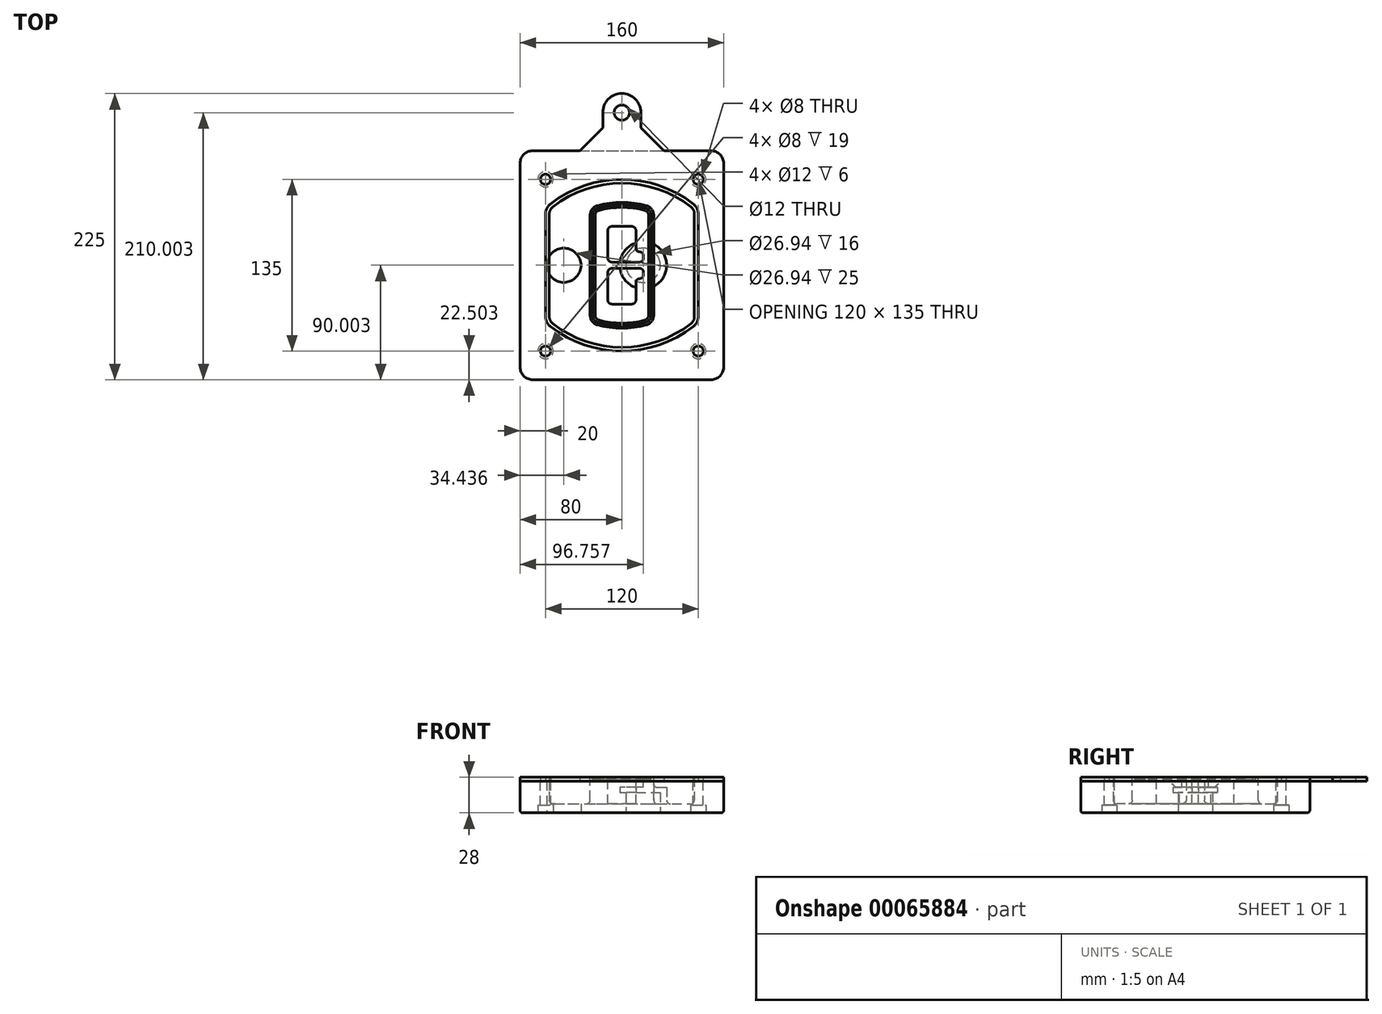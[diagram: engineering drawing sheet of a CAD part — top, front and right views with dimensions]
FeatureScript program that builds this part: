
annotation { "Feature Type Name" : "Feature", "Feature Type Description" : "" }
export const myFeature = defineFeature(function(context is Context, id is Id, definition is map)
    precondition{}
    {
        {
            var Q0;
            Q0=qCreatedBy(makeId("Top.planeOp"),FACE);
            var sketch = newSketch(context, id + "F0", { "sketchPlane" : qUnion([Q0])});
            skPoint(sketch, "E0.rect.middle", {"position": v(0, 0) * mm});
            skLineSegment(sketch, "E1.bottom", {"start": v(24.05, 28.38) * mm, "end": v(164.05, 28.38) * mm});
            skLineSegment(sketch, "E1.top", {"start": v(24.05, 208.38) * mm, "end": v(164.05, 208.38) * mm});
            skLineSegment(sketch, "E1.left", {"start": v(14.05, 38.38) * mm, "end": v(14.05, 198.38) * mm});
            skLineSegment(sketch, "E1.right", {"start": v(174.05, 38.38) * mm, "end": v(174.05, 198.38) * mm});
            skLineSegment(sketch, "E2", {"start": v(14.05, 208.38) * mm, "end": v(174.05, 28.38) * mm, "construction": true});
            skLineSegment(sketch, "E3", {"start": v(174.05, 208.38) * mm, "end": v(14.05, 28.38) * mm, "construction": true});
            skCircle(sketch, "E4", {"center": v(34.05, 185.88) * mm, "radius": 4 * mm});
            skCircle(sketch, "E5", {"center": v(154.05, 185.88) * mm, "radius": 4 * mm});
            skCircle(sketch, "E6", {"center": v(154.05, 50.88) * mm, "radius": 4 * mm});
            skCircle(sketch, "E7", {"center": v(34.05, 50.88) * mm, "radius": 4 * mm});
            skLineSegment(sketch, "E8", {"start": v(34.05, 185.88) * mm, "end": v(154.05, 185.88) * mm, "construction": true});
            skLineSegment(sketch, "E9", {"start": v(154.05, 185.88) * mm, "end": v(154.05, 50.88) * mm, "construction": true});
            skLineSegment(sketch, "E10", {"start": v(154.05, 50.88) * mm, "end": v(34.05, 50.88) * mm, "construction": true});
            skLineSegment(sketch, "E11", {"start": v(34.05, 50.88) * mm, "end": v(34.05, 185.88) * mm, "construction": true});
            skLineSegment(sketch, "E12", {"start": v(34.05, 158.68) * mm, "end": v(34.05, 78.09) * mm});
            skLineSegment(sketch, "E13", {"start": v(154.05, 158.68) * mm, "end": v(154.05, 78.09) * mm});
            skArc(sketch, "E14", {"start": v(150.2, 166.56) * mm, "mid": v(94.05, 185.88) * mm, "end": v(37.9, 166.56) * mm});
            skArc(sketch, "E15", {"start": v(37.9, 70.2) * mm, "mid": v(94.05, 50.88) * mm, "end": v(150.2, 70.2) * mm});
            skLineSegment(sketch, "E16", {"start": v(34.05, 118.38) * mm, "end": v(154.05, 118.38) * mm, "construction": true});
            skPoint(sketch, "E17.visualSharp", {"position": v(34.05, 73.38) * mm});
            skArc(sketch, "E17.filletArc", {"start": v(34.05, 78.09) * mm, "mid": v(35.06, 73.7) * mm, "end": v(37.9, 70.2) * mm});
            skPoint(sketch, "E18.visualSharp", {"position": v(34.05, 163.38) * mm});
            skArc(sketch, "E18.filletArc", {"start": v(37.9, 166.56) * mm, "mid": v(35.06, 163.06) * mm, "end": v(34.05, 158.68) * mm});
            skPoint(sketch, "E19.visualSharp", {"position": v(154.05, 163.38) * mm});
            skArc(sketch, "E19.filletArc", {"start": v(154.05, 158.68) * mm, "mid": v(153.04, 163.06) * mm, "end": v(150.2, 166.56) * mm});
            skPoint(sketch, "E20.visualSharp", {"position": v(154.05, 73.38) * mm});
            skArc(sketch, "E20.filletArc", {"start": v(150.2, 70.2) * mm, "mid": v(153.04, 73.7) * mm, "end": v(154.05, 78.09) * mm});
            skPoint(sketch, "E21.visualSharp", {"position": v(14.05, 208.38) * mm});
            skArc(sketch, "E21.filletArc", {"start": v(24.05, 208.38) * mm, "mid": v(16.98, 205.45) * mm, "end": v(14.05, 198.38) * mm});
            skPoint(sketch, "E22.visualSharp", {"position": v(174.05, 208.38) * mm});
            skArc(sketch, "E22.filletArc", {"start": v(174.05, 198.38) * mm, "mid": v(171.12, 205.45) * mm, "end": v(164.05, 208.38) * mm});
            skPoint(sketch, "E23.visualSharp", {"position": v(174.05, 28.38) * mm});
            skArc(sketch, "E23.filletArc", {"start": v(164.05, 28.38) * mm, "mid": v(171.12, 31.31) * mm, "end": v(174.05, 38.38) * mm});
            skPoint(sketch, "E24.visualSharp", {"position": v(14.05, 28.38) * mm});
            skArc(sketch, "E24.filletArc", {"start": v(14.05, 38.38) * mm, "mid": v(16.98, 31.31) * mm, "end": v(24.05, 28.38) * mm});
            skArc(sketch, "E25.0", {"start": v(151.05, 158.68) * mm, "mid": v(150.34, 161.75) * mm, "end": v(148.36, 164.2) * mm});
            skLineSegment(sketch, "E25.1", {"start": v(151.05, 158.68) * mm, "end": v(151.05, 78.09) * mm});
            skArc(sketch, "E25.2", {"start": v(148.36, 72.57) * mm, "mid": v(150.34, 75.02) * mm, "end": v(151.05, 78.09) * mm});
            skArc(sketch, "E25.3", {"start": v(39.74, 72.57) * mm, "mid": v(94.05, 53.88) * mm, "end": v(148.36, 72.57) * mm});
            skArc(sketch, "E25.4", {"start": v(37.05, 78.09) * mm, "mid": v(37.76, 75.02) * mm, "end": v(39.74, 72.57) * mm});
            skArc(sketch, "E25.5", {"start": v(148.36, 164.2) * mm, "mid": v(94.05, 182.88) * mm, "end": v(39.74, 164.2) * mm});
            skLineSegment(sketch, "E25.6", {"start": v(37.05, 158.68) * mm, "end": v(37.05, 78.09) * mm});
            skArc(sketch, "E25.7", {"start": v(39.74, 164.2) * mm, "mid": v(37.76, 161.75) * mm, "end": v(37.05, 158.68) * mm});
            skArc(sketch, "E26.0", {"start": v(35.43, 169.71) * mm, "mid": v(31.47, 164.82) * mm, "end": v(30.05, 158.68) * mm});
            skArc(sketch, "E26.1", {"start": v(152.67, 169.71) * mm, "mid": v(94.05, 189.88) * mm, "end": v(35.43, 169.71) * mm});
            skArc(sketch, "E26.2", {"start": v(158.05, 158.68) * mm, "mid": v(156.63, 164.82) * mm, "end": v(152.67, 169.71) * mm});
            skLineSegment(sketch, "E26.3", {"start": v(158.05, 158.68) * mm, "end": v(158.05, 78.09) * mm});
            skArc(sketch, "E26.4", {"start": v(152.67, 67.05) * mm, "mid": v(156.63, 71.95) * mm, "end": v(158.05, 78.09) * mm});
            skLineSegment(sketch, "E26.5", {"start": v(30.05, 158.68) * mm, "end": v(30.05, 78.09) * mm});
            skArc(sketch, "E26.6", {"start": v(35.43, 67.05) * mm, "mid": v(94.05, 46.88) * mm, "end": v(152.67, 67.05) * mm});
            skArc(sketch, "E26.7", {"start": v(30.05, 78.09) * mm, "mid": v(31.47, 71.95) * mm, "end": v(35.43, 67.05) * mm});
            skSolve(sketch);
        }
        {
            var Q0;
            Q0=makeQuery(id+"F0.imprint","IMPRINT",FACE,{"disambiguationData":[TD([[makeQuery(id+"F0.imprint","IMPRINT",EDGE,{"derivedFrom":sQuery(id+"F0.wireOp",EDGE,"E1.bottom")}),1.0]])]});
            var Q1;
            Q1=makeQuery(id+"F0.imprint","IMPRINT",FACE,{"disambiguationData":[TD([[makeQuery(id+"F0.imprint","IMPRINT",EDGE,{"derivedFrom":sQuery(id+"F0.wireOp",EDGE,"E12")}),1.0]])]});
            var Q2;
            Q2=makeQuery(id+"F0.imprint","IMPRINT",FACE,{"disambiguationData":[TD([[makeQuery(id+"F0.imprint","IMPRINT",EDGE,{"derivedFrom":sQuery(id+"F0.wireOp",EDGE,"E25.0")}),1.0]])]});
            var Q3;
            Q3=makeQuery(id+"F0.imprint","IMPRINT",FACE,{"disambiguationData":[TD([[makeQuery(id+"F0.imprint","IMPRINT",EDGE,{"derivedFrom":sQuery(id+"F0.wireOp",EDGE,"E12")}),-1.0]])]});
            extrude(context, id + "F1", {"entities" : qUnion([Q0, Q1, Q2, Q3]), "oppositeDirection" : true, "depth" : 25 * mm});
        }
        {
            var Q0;
            Q0=makeQuery(id+"F0.imprint","IMPRINT",FACE,{"disambiguationData":[TD([[makeQuery(id+"F0.imprint","IMPRINT",EDGE,{"derivedFrom":sQuery(id+"F0.wireOp",EDGE,"E12")}),1.0]])]});
            extrude(context, id + "F2", {"entities" : qUnion([Q0]), "operationType" : NewBodyOperationType.ADD, "depth" : 3 * mm});
        }
        {
            var Q0;
            Q0=makeQuery(id+"F0.imprint","IMPRINT",FACE,{"disambiguationData":[TD([[makeQuery(id+"F0.imprint","IMPRINT",EDGE,{"derivedFrom":sQuery(id+"F0.wireOp",EDGE,"E25.0")}),1.0]])]});
            extrude(context, id + "F3", {"entities" : qUnion([Q0]), "operationType" : NewBodyOperationType.REMOVE, "oppositeDirection" : true, "depth" : 18 * mm});
        }
        {
            var Q0;
            Q0=makeQuery(id+"F2.opExtrude","CAP_FACE",FACE,{"disambiguationData":[OSD([sQuery(id+"F0.wireOp",EDGE,"E12"),sQuery(id+"F0.wireOp",EDGE,"E13"),sQuery(id+"F0.wireOp",EDGE,"E14"),sQuery(id+"F0.wireOp",EDGE,"E15"),sQuery(id+"F0.wireOp",EDGE,"E17.filletArc"),sQuery(id+"F0.wireOp",EDGE,"E18.filletArc"),sQuery(id+"F0.wireOp",EDGE,"E19.filletArc"),sQuery(id+"F0.wireOp",EDGE,"E20.filletArc"),sQuery(id+"F0.wireOp",EDGE,"E25.0"),sQuery(id+"F0.wireOp",EDGE,"E25.1"),sQuery(id+"F0.wireOp",EDGE,"E25.2"),sQuery(id+"F0.wireOp",EDGE,"E25.3"),sQuery(id+"F0.wireOp",EDGE,"E25.4"),sQuery(id+"F0.wireOp",EDGE,"E25.5"),sQuery(id+"F0.wireOp",EDGE,"E25.6"),sQuery(id+"F0.wireOp",EDGE,"E25.7")])],"isStart":false});
            var sketch = newSketch(context, id + "F4", { "sketchPlane" : qUnion([Q0])});
            skArc(sketch, "E27.0", {"start": v(74.97, 71.41) * mm, "mid": v(94.05, 68.88) * mm, "end": v(113.13, 71.41) * mm});
            skArc(sketch, "E28.0", {"start": v(113.13, 165.35) * mm, "mid": v(94.05, 167.88) * mm, "end": v(74.97, 165.35) * mm});
            skLineSegment(sketch, "E29", {"start": v(69.05, 157.63) * mm, "end": v(69.05, 79.14) * mm});
            skLineSegment(sketch, "E30", {"start": v(119.05, 157.63) * mm, "end": v(119.05, 79.14) * mm});
            skLineSegment(sketch, "E31", {"start": v(69.05, 163.48) * mm, "end": v(119.05, 163.48) * mm, "construction": true});
            skLineSegment(sketch, "E32", {"start": v(69.05, 73.28) * mm, "end": v(119.05, 73.28) * mm, "construction": true});
            skPoint(sketch, "E33.visualSharp", {"position": v(69.05, 163.48) * mm});
            skArc(sketch, "E33.filletArc", {"start": v(74.97, 165.35) * mm, "mid": v(70.7, 162.5) * mm, "end": v(69.05, 157.63) * mm});
            skPoint(sketch, "E34.visualSharp", {"position": v(119.05, 163.48) * mm});
            skArc(sketch, "E34.filletArc", {"start": v(119.05, 157.63) * mm, "mid": v(117.4, 162.5) * mm, "end": v(113.13, 165.35) * mm});
            skPoint(sketch, "E35.visualSharp", {"position": v(119.05, 73.28) * mm});
            skArc(sketch, "E35.filletArc", {"start": v(113.13, 71.41) * mm, "mid": v(117.4, 74.27) * mm, "end": v(119.05, 79.14) * mm});
            skPoint(sketch, "E36.visualSharp", {"position": v(69.05, 73.28) * mm});
            skArc(sketch, "E36.filletArc", {"start": v(69.05, 79.14) * mm, "mid": v(70.7, 74.27) * mm, "end": v(74.97, 71.41) * mm});
            skArc(sketch, "E37.0", {"start": v(148.36, 164.2) * mm, "mid": v(94.05, 182.88) * mm, "end": v(39.74, 164.2) * mm});
            skArc(sketch, "E37.1", {"start": v(39.74, 164.2) * mm, "mid": v(37.76, 161.75) * mm, "end": v(37.05, 158.68) * mm});
            skLineSegment(sketch, "E37.2", {"start": v(37.05, 158.68) * mm, "end": v(37.05, 78.09) * mm});
            skArc(sketch, "E37.3", {"start": v(37.05, 78.09) * mm, "mid": v(37.76, 75.02) * mm, "end": v(39.74, 72.57) * mm});
            skArc(sketch, "E37.4", {"start": v(39.74, 72.57) * mm, "mid": v(94.05, 53.88) * mm, "end": v(148.36, 72.57) * mm});
            skArc(sketch, "E37.5", {"start": v(148.36, 72.57) * mm, "mid": v(150.34, 75.02) * mm, "end": v(151.05, 78.09) * mm});
            skLineSegment(sketch, "E37.6", {"start": v(151.05, 158.68) * mm, "end": v(151.05, 78.09) * mm});
            skArc(sketch, "E37.7", {"start": v(151.05, 158.68) * mm, "mid": v(150.34, 161.75) * mm, "end": v(148.36, 164.2) * mm});
            skLineSegment(sketch, "E38.0", {"start": v(117.05, 157.63) * mm, "end": v(117.05, 79.14) * mm});
            skArc(sketch, "E38.1", {"start": v(112.61, 73.34) * mm, "mid": v(115.81, 75.49) * mm, "end": v(117.05, 79.14) * mm});
            skArc(sketch, "E38.2", {"start": v(75.49, 73.34) * mm, "mid": v(94.05, 70.88) * mm, "end": v(112.61, 73.34) * mm});
            skArc(sketch, "E38.3", {"start": v(71.05, 79.14) * mm, "mid": v(72.29, 75.49) * mm, "end": v(75.49, 73.34) * mm});
            skLineSegment(sketch, "E38.4", {"start": v(71.05, 157.63) * mm, "end": v(71.05, 79.14) * mm});
            skArc(sketch, "E38.5", {"start": v(117.05, 157.63) * mm, "mid": v(115.81, 161.28) * mm, "end": v(112.61, 163.42) * mm});
            skArc(sketch, "E38.6", {"start": v(75.49, 163.42) * mm, "mid": v(72.29, 161.28) * mm, "end": v(71.05, 157.63) * mm});
            skArc(sketch, "E38.7", {"start": v(112.61, 163.42) * mm, "mid": v(94.05, 165.88) * mm, "end": v(75.49, 163.42) * mm});
            skArc(sketch, "E39.0", {"start": v(115.05, 157.63) * mm, "mid": v(114.23, 160.06) * mm, "end": v(112.1, 161.5) * mm});
            skLineSegment(sketch, "E39.1", {"start": v(115.05, 157.63) * mm, "end": v(115.05, 79.14) * mm});
            skArc(sketch, "E39.2", {"start": v(112.1, 75.27) * mm, "mid": v(114.23, 76.7) * mm, "end": v(115.05, 79.14) * mm});
            skArc(sketch, "E39.3", {"start": v(76, 75.27) * mm, "mid": v(94.05, 72.88) * mm, "end": v(112.1, 75.27) * mm});
            skArc(sketch, "E39.4", {"start": v(73.05, 79.14) * mm, "mid": v(73.87, 76.7) * mm, "end": v(76, 75.27) * mm});
            skArc(sketch, "E39.5", {"start": v(112.1, 161.5) * mm, "mid": v(94.05, 163.88) * mm, "end": v(76, 161.5) * mm});
            skLineSegment(sketch, "E39.6", {"start": v(73.05, 157.63) * mm, "end": v(73.05, 79.14) * mm});
            skArc(sketch, "E39.7", {"start": v(76, 161.5) * mm, "mid": v(73.87, 160.06) * mm, "end": v(73.05, 157.63) * mm});
            skLineSegment(sketch, "E40", {"start": v(69.05, 118.38) * mm, "end": v(119.05, 118.38) * mm, "construction": true});
            skLineSegment(sketch, "E41", {"start": v(83.05, 123.88) * mm, "end": v(83.05, 145.88) * mm});
            skLineSegment(sketch, "E42", {"start": v(86.05, 148.88) * mm, "end": v(102.05, 148.88) * mm});
            skLineSegment(sketch, "E43", {"start": v(105.05, 145.88) * mm, "end": v(105.05, 131.88) * mm});
            skLineSegment(sketch, "E44", {"start": v(108.05, 128.88) * mm, "end": v(108.05, 128.88) * mm});
            skLineSegment(sketch, "E45", {"start": v(111.05, 125.88) * mm, "end": v(111.05, 123.88) * mm});
            skLineSegment(sketch, "E46", {"start": v(108.05, 120.88) * mm, "end": v(86.05, 120.88) * mm});
            skPoint(sketch, "E47.visualSharp", {"position": v(83.05, 148.88) * mm});
            skArc(sketch, "E47.filletArc", {"start": v(86.05, 148.88) * mm, "mid": v(83.93, 148) * mm, "end": v(83.05, 145.88) * mm});
            skPoint(sketch, "E48.visualSharp", {"position": v(105.05, 148.88) * mm});
            skArc(sketch, "E48.filletArc", {"start": v(105.05, 145.88) * mm, "mid": v(104.17, 148) * mm, "end": v(102.05, 148.88) * mm});
            skPoint(sketch, "E49.visualSharp", {"position": v(105.05, 128.88) * mm});
            skArc(sketch, "E49.filletArc", {"start": v(105.05, 131.88) * mm, "mid": v(105.93, 129.76) * mm, "end": v(108.05, 128.88) * mm});
            skPoint(sketch, "E50.visualSharp", {"position": v(111.05, 128.88) * mm});
            skArc(sketch, "E50.filletArc", {"start": v(111.05, 125.88) * mm, "mid": v(110.17, 128) * mm, "end": v(108.05, 128.88) * mm});
            skPoint(sketch, "E51.visualSharp", {"position": v(111.05, 120.88) * mm});
            skArc(sketch, "E51.filletArc", {"start": v(108.05, 120.88) * mm, "mid": v(110.17, 121.76) * mm, "end": v(111.05, 123.88) * mm});
            skPoint(sketch, "E52.visualSharp", {"position": v(83.05, 120.88) * mm});
            skArc(sketch, "E52.filletArc", {"start": v(83.05, 123.88) * mm, "mid": v(83.93, 121.76) * mm, "end": v(86.05, 120.88) * mm});
            skLineSegment(sketch, "E53.0.MirrorCS", {"start": v(108.05, 115.88) * mm, "end": v(86.05, 115.88) * mm});
            skArc(sketch, "E54.0.MirrorCS", {"start": v(83.05, 112.88) * mm, "mid": v(83.93, 115) * mm, "end": v(86.05, 115.88) * mm});
            skLineSegment(sketch, "E55.0.MirrorCS", {"start": v(83.05, 112.88) * mm, "end": v(83.05, 90.88) * mm});
            skArc(sketch, "E56.0.MirrorCS", {"start": v(86.05, 87.88) * mm, "mid": v(83.93, 88.76) * mm, "end": v(83.05, 90.88) * mm});
            skLineSegment(sketch, "E57.0.MirrorCS", {"start": v(86.05, 87.88) * mm, "end": v(102.05, 87.88) * mm});
            skArc(sketch, "E58.0.MirrorCS", {"start": v(105.05, 90.88) * mm, "mid": v(104.17, 88.76) * mm, "end": v(102.05, 87.88) * mm});
            skLineSegment(sketch, "E59.0.MirrorCS", {"start": v(105.05, 90.88) * mm, "end": v(105.05, 104.88) * mm});
            skArc(sketch, "E60.0.MirrorCS", {"start": v(105.05, 104.88) * mm, "mid": v(105.93, 107) * mm, "end": v(108.05, 107.88) * mm});
            skArc(sketch, "E61.0.MirrorCS", {"start": v(111.05, 110.88) * mm, "mid": v(110.17, 108.76) * mm, "end": v(108.05, 107.88) * mm});
            skLineSegment(sketch, "E62.0.MirrorCS", {"start": v(111.05, 110.88) * mm, "end": v(111.05, 112.88) * mm});
            skArc(sketch, "E63.0.MirrorCS", {"start": v(108.05, 115.88) * mm, "mid": v(110.17, 115) * mm, "end": v(111.05, 112.88) * mm});
            skSolve(sketch);
        }
        {
            var Q0;
            Q0=makeQuery(id+"F4.imprint","IMPRINT",FACE,{"disambiguationData":[TD([[makeQuery(id+"F4.imprint","IMPRINT",EDGE,{"derivedFrom":sQuery(id+"F4.wireOp",EDGE,"E27.0")}),1.0]])]});
            var Q1;
            Q1=makeQuery(id+"F4.imprint","IMPRINT",FACE,{"disambiguationData":[TD([[makeQuery(id+"F4.imprint","IMPRINT",EDGE,{"derivedFrom":sQuery(id+"F4.wireOp",EDGE,"E38.0")}),-1.0]])]});
            var Q2;
            Q2=makeQuery(id+"F4.imprint","IMPRINT",FACE,{"disambiguationData":[TD([[makeQuery(id+"F4.imprint","IMPRINT",EDGE,{"derivedFrom":sQuery(id+"F4.wireOp",EDGE,"E39.0")}),1.0]])]});
            extrude(context, id + "F5", {"entities" : qUnion([Q0, Q1, Q2]), "operationType" : NewBodyOperationType.ADD, "endBound" : BoundingType.UP_TO_NEXT, "oppositeDirection" : true, "depth" : 25 * mm});
        }
        {
            var Q0;
            Q0=makeQuery(id+"F4.imprint","IMPRINT",FACE,{"disambiguationData":[TD([[makeQuery(id+"F4.imprint","IMPRINT",EDGE,{"derivedFrom":sQuery(id+"F4.wireOp",EDGE,"E38.0")}),-1.0]])]});
            extrude(context, id + "F6", {"entities" : qUnion([Q0]), "operationType" : NewBodyOperationType.REMOVE, "oppositeDirection" : true, "depth" : 2 * mm});
        }
        {
            var Q0;
            Q0=makeQuery(id+"F1.opExtrude","CAP_FACE",FACE,{"disambiguationData":[OSD([sQuery(id+"F0.wireOp",EDGE,"E1.bottom"),sQuery(id+"F0.wireOp",EDGE,"E1.top"),sQuery(id+"F0.wireOp",EDGE,"E1.left"),sQuery(id+"F0.wireOp",EDGE,"E1.right"),sQuery(id+"F0.wireOp",EDGE,"E4"),sQuery(id+"F0.wireOp",EDGE,"E5"),sQuery(id+"F0.wireOp",EDGE,"E6"),sQuery(id+"F0.wireOp",EDGE,"E7"),sQuery(id+"F0.wireOp",EDGE,"E21.filletArc"),sQuery(id+"F0.wireOp",EDGE,"E22.filletArc"),sQuery(id+"F0.wireOp",EDGE,"E23.filletArc"),sQuery(id+"F0.wireOp",EDGE,"E24.filletArc")])],"isStart":false});
            var sketch = newSketch(context, id + "F7", { "sketchPlane" : qUnion([Q0])});
            skCircle(sketch, "E64", {"center": v(110.8, -118.38) * mm, "radius": 13.47 * mm});
            skCircle(sketch, "E65", {"center": v(48.49, -118.38) * mm, "radius": 13.47 * mm});
            skLineSegment(sketch, "E66", {"start": v(174.05, -118.38) * mm, "end": v(14.05, -118.38) * mm});
            skCircle(sketch, "E67", {"center": v(110.8, -118.38) * mm, "radius": 18.47 * mm});
            skCircle(sketch, "E68", {"center": v(154.05, -185.88) * mm, "radius": 6 * mm});
            skCircle(sketch, "E69", {"center": v(34.05, -185.88) * mm, "radius": 6 * mm});
            skCircle(sketch, "E70", {"center": v(34.05, -50.88) * mm, "radius": 6 * mm});
            skCircle(sketch, "E71", {"center": v(154.05, -50.88) * mm, "radius": 6 * mm});
            skSolve(sketch);
        }
        {
            var Q0;
            {var subQ1=sQuery(id+"F7.wireOp",EDGE,"E66");var subQ4=sQuery(id+"F7.wireOp",EDGE,"E64");var subQ6=makeQuery(id+"F7.imprint","INTERSECT",VERTEX,{"disambiguationData":[OD(0.0)],"derivedFrom":[subQ4,subQ1]});Q0=makeQuery(id+"F7.imprint","IMPRINT",FACE,{"disambiguationData":[TD([[makeQuery(id+"F7.imprint","IMPRINT",EDGE,{"disambiguationData":[TD([[subQ6,-1.0]])],"derivedFrom":subQ4}),-1.0]])]});}
            var Q1;
            {var subQ0=sQuery(id+"F7.wireOp",EDGE,"E66");var subQ1=sQuery(id+"F7.wireOp",EDGE,"E64");var subQ3=makeQuery(id+"F7.imprint","INTERSECT",VERTEX,{"disambiguationData":[OD(0.0)],"derivedFrom":[subQ1,subQ0]});Q1=makeQuery(id+"F7.imprint","IMPRINT",FACE,{"disambiguationData":[TD([[makeQuery(id+"F7.imprint","IMPRINT",EDGE,{"disambiguationData":[TD([[subQ3,-1.0]])],"derivedFrom":subQ1}),1.0]])]});}
            var Q2;
            {var subQ0=sQuery(id+"F7.wireOp",EDGE,"E66");var subQ1=sQuery(id+"F7.wireOp",EDGE,"E64");var subQ3=makeQuery(id+"F7.imprint","INTERSECT",VERTEX,{"disambiguationData":[OD(0.0)],"derivedFrom":[subQ1,subQ0]});Q2=makeQuery(id+"F7.imprint","IMPRINT",FACE,{"disambiguationData":[TD([[makeQuery(id+"F7.imprint","IMPRINT",EDGE,{"disambiguationData":[TD([[subQ3,1.0]])],"derivedFrom":subQ1}),1.0]])]});}
            var Q3;
            {var subQ1=sQuery(id+"F7.wireOp",EDGE,"E66");var subQ4=sQuery(id+"F7.wireOp",EDGE,"E64");var subQ6=makeQuery(id+"F7.imprint","INTERSECT",VERTEX,{"disambiguationData":[OD(0.0)],"derivedFrom":[subQ4,subQ1]});Q3=makeQuery(id+"F7.imprint","IMPRINT",FACE,{"disambiguationData":[TD([[makeQuery(id+"F7.imprint","IMPRINT",EDGE,{"disambiguationData":[TD([[subQ6,1.0]])],"derivedFrom":subQ4}),-1.0]])]});}
            extrude(context, id + "F8", {"entities" : qUnion([Q0, Q1, Q2, Q3]), "operationType" : NewBodyOperationType.ADD, "oppositeDirection" : true, "depth" : 20 * mm});
        }
        {
            var Q0;
            {var subQ0=sQuery(id+"F7.wireOp",EDGE,"E66");var subQ1=sQuery(id+"F7.wireOp",EDGE,"E64");var subQ3=makeQuery(id+"F7.imprint","INTERSECT",VERTEX,{"disambiguationData":[OD(0.0)],"derivedFrom":[subQ1,subQ0]});Q0=makeQuery(id+"F7.imprint","IMPRINT",FACE,{"disambiguationData":[TD([[makeQuery(id+"F7.imprint","IMPRINT",EDGE,{"disambiguationData":[TD([[subQ3,-1.0]])],"derivedFrom":subQ1}),1.0]])]});}
            var Q1;
            {var subQ0=sQuery(id+"F7.wireOp",EDGE,"E66");var subQ1=sQuery(id+"F7.wireOp",EDGE,"E64");var subQ3=makeQuery(id+"F7.imprint","INTERSECT",VERTEX,{"disambiguationData":[OD(0.0)],"derivedFrom":[subQ1,subQ0]});Q1=makeQuery(id+"F7.imprint","IMPRINT",FACE,{"disambiguationData":[TD([[makeQuery(id+"F7.imprint","IMPRINT",EDGE,{"disambiguationData":[TD([[subQ3,1.0]])],"derivedFrom":subQ1}),1.0]])]});}
            extrude(context, id + "F9", {"entities" : qUnion([Q0, Q1]), "operationType" : NewBodyOperationType.REMOVE, "oppositeDirection" : true, "depth" : 16 * mm});
        }
        {
            var Q0;
            {var subQ0=sQuery(id+"F7.wireOp",EDGE,"E66");var subQ1=sQuery(id+"F7.wireOp",EDGE,"E65");var subQ3=makeQuery(id+"F7.imprint","INTERSECT",VERTEX,{"disambiguationData":[OD(0.0)],"derivedFrom":[subQ1,subQ0]});Q0=makeQuery(id+"F7.imprint","IMPRINT",FACE,{"disambiguationData":[TD([[makeQuery(id+"F7.imprint","IMPRINT",EDGE,{"disambiguationData":[TD([[subQ3,-1.0]])],"derivedFrom":subQ1}),1.0]])]});}
            var Q1;
            {var subQ0=sQuery(id+"F7.wireOp",EDGE,"E66");var subQ1=sQuery(id+"F7.wireOp",EDGE,"E65");var subQ3=makeQuery(id+"F7.imprint","INTERSECT",VERTEX,{"disambiguationData":[OD(0.0)],"derivedFrom":[subQ1,subQ0]});Q1=makeQuery(id+"F7.imprint","IMPRINT",FACE,{"disambiguationData":[TD([[makeQuery(id+"F7.imprint","IMPRINT",EDGE,{"disambiguationData":[TD([[subQ3,1.0]])],"derivedFrom":subQ1}),1.0]])]});}
            extrude(context, id + "F10", {"entities" : qUnion([Q0, Q1]), "operationType" : NewBodyOperationType.REMOVE, "oppositeDirection" : true, "depth" : 25 * mm});
        }
        {
            var Q0;
            Q0=makeQuery(id+"F7.imprint","IMPRINT",FACE,{"disambiguationData":[TD([[makeQuery(id+"F7.imprint","IMPRINT",EDGE,{"derivedFrom":sQuery(id+"F7.wireOp",EDGE,"E68")}),1.0]])]});
            var Q1;
            Q1=makeQuery(id+"F7.imprint","IMPRINT",FACE,{"disambiguationData":[TD([[makeQuery(id+"F7.imprint","IMPRINT",EDGE,{"derivedFrom":makeQuery(id+"F1.opExtrude","CAP_EDGE",EDGE,{"disambiguationData":[OSD([sQuery(id+"F0.wireOp",EDGE,"E5")])],"isStart":false})}),-1.0]])]});
            var Q2;
            Q2=makeQuery(id+"F7.imprint","IMPRINT",FACE,{"disambiguationData":[TD([[makeQuery(id+"F7.imprint","IMPRINT",EDGE,{"derivedFrom":sQuery(id+"F7.wireOp",EDGE,"E69")}),1.0]])]});
            var Q3;
            Q3=makeQuery(id+"F7.imprint","IMPRINT",FACE,{"disambiguationData":[TD([[makeQuery(id+"F7.imprint","IMPRINT",EDGE,{"derivedFrom":makeQuery(id+"F1.opExtrude","CAP_EDGE",EDGE,{"disambiguationData":[OSD([sQuery(id+"F0.wireOp",EDGE,"E4")])],"isStart":false})}),-1.0]])]});
            var Q4;
            Q4=makeQuery(id+"F7.imprint","IMPRINT",FACE,{"disambiguationData":[TD([[makeQuery(id+"F7.imprint","IMPRINT",EDGE,{"derivedFrom":sQuery(id+"F7.wireOp",EDGE,"E70")}),1.0]])]});
            var Q5;
            Q5=makeQuery(id+"F7.imprint","IMPRINT",FACE,{"disambiguationData":[TD([[makeQuery(id+"F7.imprint","IMPRINT",EDGE,{"derivedFrom":makeQuery(id+"F1.opExtrude","CAP_EDGE",EDGE,{"disambiguationData":[OSD([sQuery(id+"F0.wireOp",EDGE,"E7")])],"isStart":false})}),-1.0]])]});
            var Q6;
            Q6=makeQuery(id+"F7.imprint","IMPRINT",FACE,{"disambiguationData":[TD([[makeQuery(id+"F7.imprint","IMPRINT",EDGE,{"derivedFrom":sQuery(id+"F7.wireOp",EDGE,"E71")}),1.0]])]});
            var Q7;
            Q7=makeQuery(id+"F7.imprint","IMPRINT",FACE,{"disambiguationData":[TD([[makeQuery(id+"F7.imprint","IMPRINT",EDGE,{"derivedFrom":makeQuery(id+"F1.opExtrude","CAP_EDGE",EDGE,{"disambiguationData":[OSD([sQuery(id+"F0.wireOp",EDGE,"E6")])],"isStart":false})}),-1.0]])]});
            extrude(context, id + "F11", {"entities" : qUnion([Q0, Q1, Q2, Q3, Q4, Q5, Q6, Q7]), "operationType" : NewBodyOperationType.REMOVE, "oppositeDirection" : true, "depth" : 6 * mm});
        }
        {
            var Q0;
            Q0=makeQuery(id+"F9.boolean.opBoolean","COPY",FACE,{"derivedFrom":makeQuery(id+"F9.opExtrude","CAP_FACE",FACE,{"disambiguationData":[OSD([sQuery(id+"F7.wireOp",EDGE,"E64")])],"isStart":false})});
            var sketch = newSketch(context, id + "F12", { "sketchPlane" : qUnion([Q0])});
            skArc(sketch, "E72.0", {"start": v(105.05, -100.83) * mm, "mid": v(96.62, -106.56) * mm, "end": v(92.5, -115.88) * mm});
            skArc(sketch, "E72.1", {"start": v(92.5, -120.88) * mm, "mid": v(96.62, -130.2) * mm, "end": v(105.05, -135.93) * mm});
            skLineSegment(sketch, "E73", {"start": v(92.5, -120.88) * mm, "end": v(108.05, -120.88) * mm});
            skLineSegment(sketch, "E74.0", {"start": v(108.05, -115.88) * mm, "end": v(92.5, -115.88) * mm});
            skArc(sketch, "E74.1", {"start": v(108.05, -115.88) * mm, "mid": v(110.17, -115) * mm, "end": v(111.05, -112.88) * mm});
            skLineSegment(sketch, "E74.2", {"start": v(111.05, -110.88) * mm, "end": v(111.05, -112.88) * mm});
            skArc(sketch, "E74.3", {"start": v(111.05, -110.88) * mm, "mid": v(110.17, -108.76) * mm, "end": v(108.05, -107.88) * mm});
            skArc(sketch, "E74.4", {"start": v(105.05, -104.88) * mm, "mid": v(105.93, -107) * mm, "end": v(108.05, -107.88) * mm});
            skLineSegment(sketch, "E74.5", {"start": v(105.05, -100.83) * mm, "end": v(105.05, -104.88) * mm});
            skLineSegment(sketch, "E74.7", {"start": v(108.05, -120.88) * mm, "end": v(92.5, -120.88) * mm});
            skArc(sketch, "E74.8", {"start": v(108.05, -120.88) * mm, "mid": v(110.17, -121.76) * mm, "end": v(111.05, -123.88) * mm});
            skLineSegment(sketch, "E74.9", {"start": v(111.05, -125.88) * mm, "end": v(111.05, -123.88) * mm});
            skArc(sketch, "E74.10", {"start": v(111.05, -125.88) * mm, "mid": v(110.17, -128) * mm, "end": v(108.05, -128.88) * mm});
            skArc(sketch, "E74.11", {"start": v(105.05, -131.88) * mm, "mid": v(105.93, -129.76) * mm, "end": v(108.05, -128.88) * mm});
            skLineSegment(sketch, "E74.12", {"start": v(105.05, -135.93) * mm, "end": v(105.05, -131.88) * mm});
            skPoint(sketch, "E75.orphan", {"position": v(105.05, -145.88) * mm});
            skPoint(sketch, "E76.orphan", {"position": v(86.05, -120.88) * mm});
            skPoint(sketch, "E77.orphan", {"position": v(86.05, -115.88) * mm});
            skPoint(sketch, "E78.orphan", {"position": v(105.05, -90.88) * mm});
            skSolve(sketch);
        }
        {
            var Q0;
            {var subQ7=sQuery(id+"F12.wireOp",EDGE,"E72.0");var subQ14=sQuery(id+"F12.wireOp",EDGE,"E72.1");var subQ16=sQuery(id+"F12.wireOp",EDGE,"E74.1");var subQ18=sQuery(id+"F12.wireOp",EDGE,"E74.8");Q0=qUnion([makeQuery(id+"F12.imprint","IMPRINT",FACE,{"disambiguationData":[TD([[makeQuery(id+"F12.imprint","IMPRINT",EDGE,{"derivedFrom":subQ7}),1.0]])]}),makeQuery(id+"F12.imprint","IMPRINT",FACE,{"disambiguationData":[TD([[makeQuery(id+"F12.imprint","IMPRINT",EDGE,{"derivedFrom":subQ14}),1.0]])]}),makeQuery(id+"F12.imprint","IMPRINT",FACE,{"disambiguationData":[TD([[makeQuery(id+"F12.imprint","IMPRINT",EDGE,{"derivedFrom":subQ16}),1.0]])]}),makeQuery(id+"F12.imprint","IMPRINT",FACE,{"disambiguationData":[TD([[makeQuery(id+"F12.imprint","IMPRINT",EDGE,{"derivedFrom":subQ18}),-1.0]])]})]);}
            var Q1;
            Q1=makeQuery(id+"F5.boolean.opBoolean","SPLIT",FACE,{"disambiguationData":[TD([makeQuery(id+"F5.opExtrude","SWEPT_FACE",FACE,{"disambiguationData":[OSD([sQuery(id+"F4.wireOp",EDGE,"E41")])]})])],"derivedFrom":makeQuery(id+"F3.boolean.opBoolean","COPY",FACE,{"derivedFrom":makeQuery(id+"F3.opExtrude","CAP_FACE",FACE,{"disambiguationData":[OSD([sQuery(id+"F0.wireOp",EDGE,"E25.0"),sQuery(id+"F0.wireOp",EDGE,"E25.1"),sQuery(id+"F0.wireOp",EDGE,"E25.2"),sQuery(id+"F0.wireOp",EDGE,"E25.3"),sQuery(id+"F0.wireOp",EDGE,"E25.4"),sQuery(id+"F0.wireOp",EDGE,"E25.5"),sQuery(id+"F0.wireOp",EDGE,"E25.6"),sQuery(id+"F0.wireOp",EDGE,"E25.7")])],"isStart":false})})});
            extrude(context, id + "F13", {"entities" : qUnion([Q0]), "operationType" : NewBodyOperationType.REMOVE, "endBound" : BoundingType.UP_TO_SURFACE, "endBoundEntityFace" : qUnion([Q1]), "depth" : 25 * mm});
        }
        {
            var Q0;
            Q0=makeQuery(id+"F3.boolean.opBoolean","COPY",EDGE,{"derivedFrom":makeQuery(id+"F3.opExtrude","CAP_EDGE",EDGE,{"disambiguationData":[OSD([sQuery(id+"F0.wireOp",EDGE,"E25.6")])],"isStart":false})});
            var Q1;
            Q1=makeQuery(id+"F8.boolean.opBoolean","INTERSECT",EDGE,{"derivedFrom":[makeQuery(id+"F5.opExtrude","SWEPT_FACE",FACE,{"disambiguationData":[OSD([sQuery(id+"F4.wireOp",EDGE,"E30")])]}),makeQuery(id+"F8.opExtrude","CAP_FACE",FACE,{"disambiguationData":[OSD([sQuery(id+"F7.wireOp",EDGE,"E67")])],"isStart":false})]});
            var Q2;
            Q2=makeQuery(id+"F8.boolean.opBoolean","INTERSECT",EDGE,{"disambiguationData":[OD(1.0)],"derivedFrom":[makeQuery(id+"F5.opExtrude","SWEPT_FACE",FACE,{"disambiguationData":[OSD([sQuery(id+"F4.wireOp",EDGE,"E30")])]}),makeQuery(id+"F8.opExtrude","SWEPT_FACE",FACE,{"disambiguationData":[OSD([sQuery(id+"F7.wireOp",EDGE,"E67")])]})]});
            var Q3;
            {var subQ0=sQuery(id+"F4.wireOp",EDGE,"E30");Q3=makeQuery(id+"F8.boolean.opBoolean","SPLIT",EDGE,{"disambiguationData":[TD([makeQuery(id+"F5.opExtrude","SWEPT_FACE",FACE,{"disambiguationData":[OSD([sQuery(id+"F4.wireOp",EDGE,"E35.filletArc")])]})])],"derivedFrom":makeQuery(id+"F5.opExtrude","CAP_EDGE",EDGE,{"disambiguationData":[OSD([subQ0])],"isStart":false})});}
            var Q4;
            {var subQ0=sQuery(id+"F0.wireOp",EDGE,"E25.7");var subQ1=sQuery(id+"F0.wireOp",EDGE,"E25.1");var subQ2=sQuery(id+"F0.wireOp",EDGE,"E25.6");var subQ3=sQuery(id+"F0.wireOp",EDGE,"E25.5");var subQ4=sQuery(id+"F0.wireOp",EDGE,"E25.4");var subQ5=sQuery(id+"F0.wireOp",EDGE,"E25.0");var subQ6=sQuery(id+"F0.wireOp",EDGE,"E25.2");var subQ7=sQuery(id+"F0.wireOp",EDGE,"E25.3");Q4=makeQuery(id+"F8.boolean.opBoolean","INTERSECT",EDGE,{"derivedFrom":[makeQuery(id+"F5.boolean.opBoolean","SPLIT",FACE,{"disambiguationData":[TD([makeQuery(id+"F2.opExtrude","SWEPT_FACE",FACE,{"disambiguationData":[OSD([subQ5])]})])],"derivedFrom":makeQuery(id+"F3.boolean.opBoolean","COPY",FACE,{"derivedFrom":makeQuery(id+"F3.opExtrude","CAP_FACE",FACE,{"disambiguationData":[OSD([subQ5,subQ1,subQ6,subQ7,subQ4,subQ3,subQ2,subQ0])],"isStart":false})})}),makeQuery(id+"F8.opExtrude","SWEPT_FACE",FACE,{"disambiguationData":[OSD([sQuery(id+"F7.wireOp",EDGE,"E67")])]})]});}
            var Q5;
            Q5=makeQuery(id+"F8.boolean.opBoolean","INTERSECT",EDGE,{"disambiguationData":[OD(0.0)],"derivedFrom":[makeQuery(id+"F5.opExtrude","SWEPT_FACE",FACE,{"disambiguationData":[OSD([sQuery(id+"F4.wireOp",EDGE,"E30")])]}),makeQuery(id+"F8.opExtrude","SWEPT_FACE",FACE,{"disambiguationData":[OSD([sQuery(id+"F7.wireOp",EDGE,"E67")])]})]});
            fillet(context, id + "F14", {"entities" : qUnion([Q0, Q1, Q2, Q3, Q4, Q5]), "radius" : 3 * mm, "tangentPropagation" : true, "allowEdgeOverflow" : false});
        }
        {
            var Q0;
            Q0=makeQuery(id+"F1.opExtrude","CAP_EDGE",EDGE,{"disambiguationData":[OSD([sQuery(id+"F0.wireOp",EDGE,"E1.bottom")])],"isStart":false});
            fillet(context, id + "F15", {"entities" : qUnion([Q0]), "radius" : 2 * mm, "tangentPropagation" : true, "allowEdgeOverflow" : false});
        }
        {
            var Q0;
            {var subQ0=sQuery(id+"F0.wireOp",EDGE,"E22.filletArc");var subQ1=sQuery(id+"F0.wireOp",EDGE,"E7");var subQ2=sQuery(id+"F0.wireOp",EDGE,"E6");var subQ3=sQuery(id+"F0.wireOp",EDGE,"E5");var subQ4=sQuery(id+"F0.wireOp",EDGE,"E4");var subQ5=sQuery(id+"F0.wireOp",EDGE,"E1.bottom");var subQ6=sQuery(id+"F0.wireOp",EDGE,"E21.filletArc");var subQ7=sQuery(id+"F0.wireOp",EDGE,"E1.top");var subQ8=sQuery(id+"F0.wireOp",EDGE,"E1.left");var subQ9=sQuery(id+"F0.wireOp",EDGE,"E1.right");var subQ10=sQuery(id+"F0.wireOp",EDGE,"E23.filletArc");var subQ11=sQuery(id+"F0.wireOp",EDGE,"E24.filletArc");Q0=makeQuery(id+"F2.boolean.opBoolean","SPLIT",FACE,{"disambiguationData":[TD([makeQuery(id+"F1.opExtrude","SWEPT_FACE",FACE,{"disambiguationData":[OSD([subQ5])]})])],"derivedFrom":makeQuery(id+"F1.opExtrude","CAP_FACE",FACE,{"disambiguationData":[OSD([subQ5,subQ7,subQ8,subQ9,subQ4,subQ3,subQ2,subQ1,subQ6,subQ0,subQ10,subQ11])],"isStart":true})});}
            var sketch = newSketch(context, id + "F16", { "sketchPlane" : qUnion([Q0])});
            skLineSegment(sketch, "E79", {"start": v(61.05, 208.38) * mm, "end": v(79.05, 226.38) * mm});
            skLineSegment(sketch, "E80", {"start": v(79.05, 226.38) * mm, "end": v(79.05, 238.38) * mm});
            skLineSegment(sketch, "E81", {"start": v(94.05, 208.38) * mm, "end": v(94.05, 238.38) * mm, "construction": true});
            skLineSegment(sketch, "E82.MirrorCS", {"start": v(109.05, 226.38) * mm, "end": v(109.05, 238.38) * mm});
            skLineSegment(sketch, "E83.MirrorCS", {"start": v(127.05, 208.38) * mm, "end": v(109.05, 226.38) * mm});
            skArc(sketch, "E84", {"start": v(109.05, 238.38) * mm, "mid": v(94.05, 253.38) * mm, "end": v(79.05, 238.38) * mm});
            skCircle(sketch, "E85", {"center": v(94.05, 238.38) * mm, "radius": 6 * mm});
            skLineSegment(sketch, "E86", {"start": v(14.05, 118.38) * mm, "end": v(174.05, 118.38) * mm, "construction": true});
            skArc(sketch, "E87.MirrorCS", {"start": v(79.05, 238.38) * mm, "mid": v(94.05, 253.38) * mm, "end": v(109.05, 238.38) * mm});
            skLineSegment(sketch, "E88.MirrorCS", {"start": v(174.05, 118.38) * mm, "end": v(14.05, 118.38) * mm, "construction": true});
            skLineSegment(sketch, "E89.MirrorCS", {"start": v(109.05, 10.38) * mm, "end": v(109.05, -1.62) * mm});
            skCircle(sketch, "E90.MirrorC", {"center": v(94.05, -1.62) * mm, "radius": 6 * mm});
            skLineSegment(sketch, "E91.MirrorCS", {"start": v(79.05, 10.38) * mm, "end": v(79.05, -1.62) * mm});
            skArc(sketch, "E92.MirrorCS", {"start": v(109.05, -1.62) * mm, "mid": v(94.05, -16.62) * mm, "end": v(79.05, -1.62) * mm});
            skArc(sketch, "E93.MirrorCS", {"start": v(79.05, -1.62) * mm, "mid": v(94.05, -16.62) * mm, "end": v(109.05, -1.62) * mm});
            skLineSegment(sketch, "E94.MirrorCS", {"start": v(127.05, 28.38) * mm, "end": v(109.05, 10.38) * mm});
            skLineSegment(sketch, "E95.MirrorCS", {"start": v(61.05, 28.38) * mm, "end": v(79.05, 10.38) * mm});
            skLineSegment(sketch, "E96.MirrorCS", {"start": v(94.05, 28.38) * mm, "end": v(94.05, -1.62) * mm, "construction": true});
            skSolve(sketch);
        }
        {
            var Q0;
            Q0=makeQuery(id+"F16.imprint","IMPRINT",FACE,{"disambiguationData":[TD([[makeQuery(id+"F16.imprint","IMPRINT",EDGE,{"derivedFrom":sQuery(id+"F16.wireOp",EDGE,"E92.MirrorCS")}),-1.0]])]});
            var Q1;
            Q1=makeQuery(id+"F16.imprint","IMPRINT",FACE,{"disambiguationData":[TD([[makeQuery(id+"F16.imprint","IMPRINT",EDGE,{"derivedFrom":sQuery(id+"F16.wireOp",EDGE,"E80")}),-1.0]])]});
            var Q2;
            Q2=makeQuery(id+"F16.imprint","IMPRINT",FACE,{"disambiguationData":[TD([[makeQuery(id+"F16.imprint","IMPRINT",EDGE,{"derivedFrom":makeQuery(id+"F1.opExtrude","CAP_EDGE",EDGE,{"disambiguationData":[OSD([sQuery(id+"F0.wireOp",EDGE,"E1.left")])],"isStart":true})}),-1.0]])]});
            var Q3;
            Q3=makeQuery(id+"F2.opExtrude","CAP_FACE",FACE,{"disambiguationData":[OSD([sQuery(id+"F0.wireOp",EDGE,"E12"),sQuery(id+"F0.wireOp",EDGE,"E13"),sQuery(id+"F0.wireOp",EDGE,"E14"),sQuery(id+"F0.wireOp",EDGE,"E15"),sQuery(id+"F0.wireOp",EDGE,"E17.filletArc"),sQuery(id+"F0.wireOp",EDGE,"E18.filletArc"),sQuery(id+"F0.wireOp",EDGE,"E19.filletArc"),sQuery(id+"F0.wireOp",EDGE,"E20.filletArc"),sQuery(id+"F0.wireOp",EDGE,"E25.0"),sQuery(id+"F0.wireOp",EDGE,"E25.1"),sQuery(id+"F0.wireOp",EDGE,"E25.2"),sQuery(id+"F0.wireOp",EDGE,"E25.3"),sQuery(id+"F0.wireOp",EDGE,"E25.4"),sQuery(id+"F0.wireOp",EDGE,"E25.5"),sQuery(id+"F0.wireOp",EDGE,"E25.6"),sQuery(id+"F0.wireOp",EDGE,"E25.7")])],"isStart":false});
            extrude(context, id + "F17", {"entities" : qUnion([Q0, Q1, Q2]), "endBound" : BoundingType.UP_TO_SURFACE, "endBoundEntityFace" : qUnion([Q3]), "depth" : 25 * mm});
        }
    });
